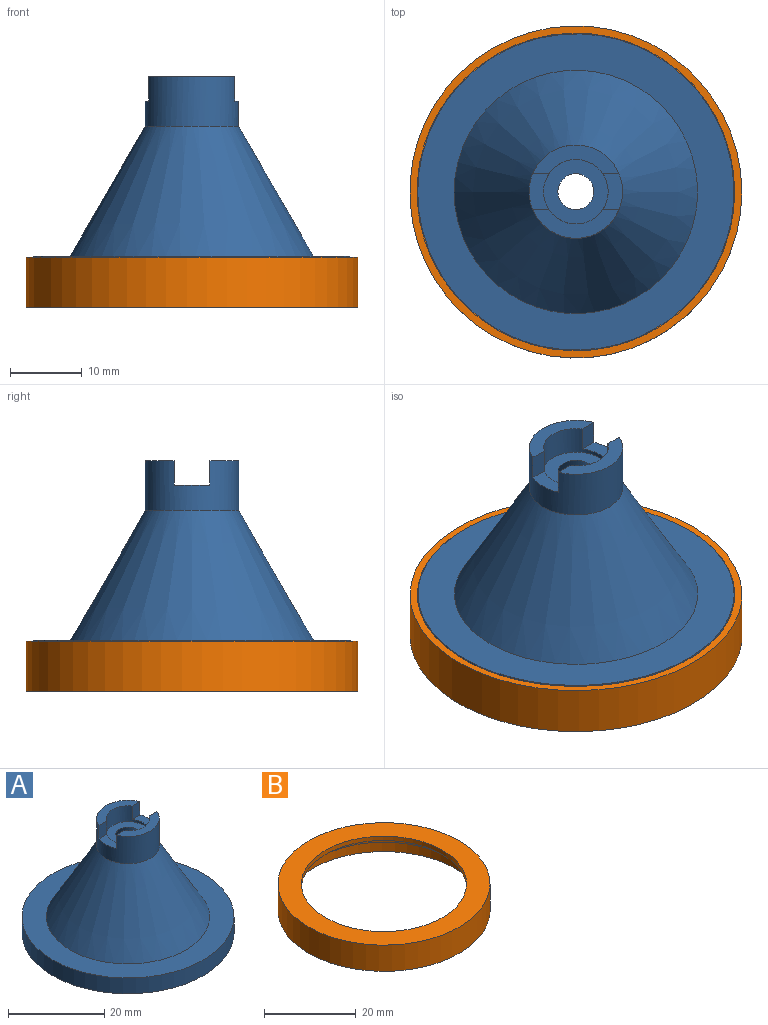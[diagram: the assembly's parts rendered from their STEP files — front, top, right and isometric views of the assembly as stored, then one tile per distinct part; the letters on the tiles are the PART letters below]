
ASSEMBLY  parts=2 mates=1
PART A: 18 faces, bbox 44x44x29 mm
  f0: cylinder r=4.5mm len=9mm, axis (0,0,-1), area 77mm2, adj f1,f6,f7,f12,f13,f14,f15,f16
  f1: plane 12x4mm, normal (0,0,1), area 24.2mm2, adj f0,f2,f14,f15
  f2: cylinder r=6.5mm len=13mm, axis (0,0,-1), area 248.1mm2, adj f1,f7,f8,f12,f13,f14,f15,f16
  f3: cylinder r=20mm len=40mm, axis (0,0,-1), area 188.5mm2, adj f4,f11
  f4: cone r=15.62mm half-angle=80deg, axis (0,0,-1), area 497.5mm2, adj f3,f5
  f5: cone r=2.5mm half-angle=30deg, axis (0,0,-1), area 1494.1mm2, adj f4,f6
  f6: plane 9x9mm, normal (0,0,1), area 44mm2, adj f0,f5
  f7: plane 12x4mm, normal (0,0,1), area 24.2mm2, adj f0,f2,f12,f16
  f8: cone r=16.93mm half-angle=30deg, axis (0,0,-1), area 1536.3mm2, adj f2,f9
  f9: plane 44x44mm, normal (0,0,1), area 619.7mm2, adj f8,f10
  f10: cylinder r=22mm len=44mm, axis (0,0,-1), area 552.9mm2, adj f9,f11
  f11: plane 44x44mm, normal (0,0,-1), area 263.9mm2, adj f3,f10
  f12: plane 3.4x2.26mm, normal (0,-1,0), area 7.7mm2, adj f0,f2,f7,f13
  f13: plane 5x2.76mm, normal (0,0,1), area 10.4mm2, adj f0,f2,f12,f14
  f14: plane 3.4x2.26mm, normal (0,1,0), area 7.7mm2, adj f0,f1,f2,f13
  f15: plane 3.4x2.26mm, normal (0,1,0), area 7.7mm2, adj f0,f1,f2,f17
  f16: plane 3.4x2.26mm, normal (0,-1,0), area 7.7mm2, adj f0,f2,f7,f17
  f17: plane 5x2.76mm, normal (0,0,1), area 10.4mm2, adj f0,f2,f15,f16
PART B: 8 faces, bbox 46.2x46.2x7 mm
  f0: cylinder r=23.1mm len=46.2mm, axis (0,0,-1), area 1016mm2, adj f1,f7
  f1: plane 46.2x46.2mm, normal (0,0,-1), area 142mm2, adj f0,f2
  f2: cylinder r=22.1mm len=44.2mm, axis (0,0,-1), area 555.4mm2, adj f1,f3
  f3: plane 44.2x44.2mm, normal (0,0,-1), area 277.7mm2, adj f2,f4
  f4: cylinder r=20mm len=40mm, axis (0,0,-1), area 188.5mm2, adj f3,f5
  f5: cone r=18mm half-angle=80deg, axis (0,0,-1), area 242.4mm2, adj f4,f6
  f6: cylinder r=18mm len=36mm, axis (0,0,-1), area 129.8mm2, adj f5,f7
  f7: plane 46.2x46.2mm, normal (0,0,1), area 658.5mm2, adj f0,f6
PLACE A t=(-14.56,1.37,-24.92)mm
PLACE B rot(axis=(0,-1,0),180deg) t=(-59.93,1.37,-21.04)mm
MATE slider A.f0 <-> B.f0  axis (0,0,-1) through (-14.56,1.37,-24.92)mm
